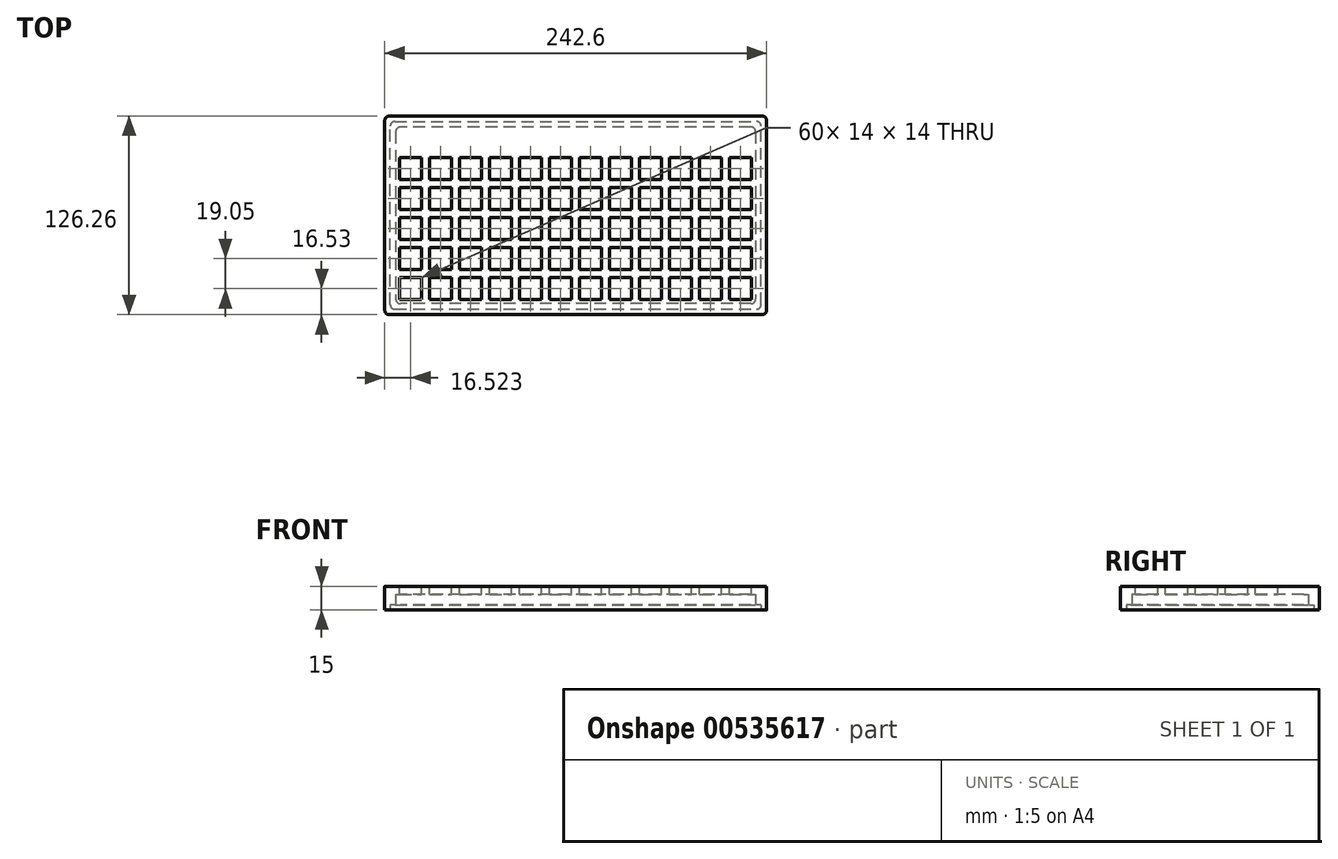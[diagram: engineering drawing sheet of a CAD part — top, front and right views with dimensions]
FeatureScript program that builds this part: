
annotation { "Feature Type Name" : "Feature", "Feature Type Description" : "" }
export const myFeature = defineFeature(function(context is Context, id is Id, definition is map)
    precondition{}
    {
        {
            var Q0;
            Q0=qCreatedBy(makeId("Top.planeOp"),FACE);
            var sketch = newSketch(context, id + "F0", { "sketchPlane" : qUnion([Q0])});
            skLineSegment(sketch, "E0", {"start": v(-121.3, 63.13) * mm, "end": v(121.3, 63.13) * mm});
            skLineSegment(sketch, "E1", {"start": v(121.3, 63.13) * mm, "end": v(121.3, -63.13) * mm});
            skLineSegment(sketch, "E2", {"start": v(121.3, -63.13) * mm, "end": v(-121.3, -63.13) * mm});
            skLineSegment(sketch, "E3", {"start": v(-121.3, -63.13) * mm, "end": v(-121.3, 63.13) * mm});
            skLineSegment(sketch, "E4", {"start": v(-111.78, -39.6) * mm, "end": v(-97.78, -39.6) * mm});
            skLineSegment(sketch, "E5", {"start": v(-97.78, -39.6) * mm, "end": v(-97.78, -53.6) * mm});
            skLineSegment(sketch, "E6", {"start": v(-97.78, -53.6) * mm, "end": v(-111.78, -53.6) * mm});
            skLineSegment(sketch, "E7", {"start": v(-111.78, -53.6) * mm, "end": v(-111.78, -39.6) * mm});
            skLineSegment(sketch, "E8", {"start": v(-92.73, -39.6) * mm, "end": v(-78.73, -39.6) * mm});
            skLineSegment(sketch, "E9", {"start": v(-78.73, -39.6) * mm, "end": v(-78.73, -53.6) * mm});
            skLineSegment(sketch, "E10", {"start": v(-78.73, -53.6) * mm, "end": v(-92.73, -53.6) * mm});
            skLineSegment(sketch, "E11", {"start": v(-92.73, -53.6) * mm, "end": v(-92.73, -39.6) * mm});
            skLineSegment(sketch, "E12", {"start": v(-73.68, -39.6) * mm, "end": v(-59.68, -39.6) * mm});
            skLineSegment(sketch, "E13", {"start": v(-59.68, -39.6) * mm, "end": v(-59.68, -53.6) * mm});
            skLineSegment(sketch, "E14", {"start": v(-59.68, -53.6) * mm, "end": v(-73.68, -53.6) * mm});
            skLineSegment(sketch, "E15", {"start": v(-73.68, -53.6) * mm, "end": v(-73.68, -39.6) * mm});
            skLineSegment(sketch, "E16", {"start": v(-54.63, -39.6) * mm, "end": v(-40.63, -39.6) * mm});
            skLineSegment(sketch, "E17", {"start": v(-40.63, -39.6) * mm, "end": v(-40.63, -53.6) * mm});
            skLineSegment(sketch, "E18", {"start": v(-40.63, -53.6) * mm, "end": v(-54.63, -53.6) * mm});
            skLineSegment(sketch, "E19", {"start": v(-54.63, -53.6) * mm, "end": v(-54.63, -39.6) * mm});
            skLineSegment(sketch, "E20", {"start": v(-35.58, -39.6) * mm, "end": v(-21.58, -39.6) * mm});
            skLineSegment(sketch, "E21", {"start": v(-21.58, -39.6) * mm, "end": v(-21.58, -53.6) * mm});
            skLineSegment(sketch, "E22", {"start": v(-21.58, -53.6) * mm, "end": v(-35.58, -53.6) * mm});
            skLineSegment(sketch, "E23", {"start": v(-35.58, -53.6) * mm, "end": v(-35.58, -39.6) * mm});
            skLineSegment(sketch, "E24", {"start": v(-16.53, -39.6) * mm, "end": v(-2.53, -39.6) * mm});
            skLineSegment(sketch, "E25", {"start": v(-2.53, -39.6) * mm, "end": v(-2.53, -53.6) * mm});
            skLineSegment(sketch, "E26", {"start": v(-2.53, -53.6) * mm, "end": v(-16.53, -53.6) * mm});
            skLineSegment(sketch, "E27", {"start": v(-16.53, -53.6) * mm, "end": v(-16.53, -39.6) * mm});
            skLineSegment(sketch, "E28", {"start": v(2.52, -39.6) * mm, "end": v(16.52, -39.6) * mm});
            skLineSegment(sketch, "E29", {"start": v(16.52, -39.6) * mm, "end": v(16.52, -53.6) * mm});
            skLineSegment(sketch, "E30", {"start": v(16.52, -53.6) * mm, "end": v(2.52, -53.6) * mm});
            skLineSegment(sketch, "E31", {"start": v(2.52, -53.6) * mm, "end": v(2.52, -39.6) * mm});
            skLineSegment(sketch, "E32", {"start": v(21.57, -39.6) * mm, "end": v(35.57, -39.6) * mm});
            skLineSegment(sketch, "E33", {"start": v(35.57, -39.6) * mm, "end": v(35.57, -53.6) * mm});
            skLineSegment(sketch, "E34", {"start": v(35.57, -53.6) * mm, "end": v(21.57, -53.6) * mm});
            skLineSegment(sketch, "E35", {"start": v(21.57, -53.6) * mm, "end": v(21.57, -39.6) * mm});
            skLineSegment(sketch, "E36", {"start": v(40.62, -39.6) * mm, "end": v(54.62, -39.6) * mm});
            skLineSegment(sketch, "E37", {"start": v(54.62, -39.6) * mm, "end": v(54.62, -53.6) * mm});
            skLineSegment(sketch, "E38", {"start": v(54.62, -53.6) * mm, "end": v(40.62, -53.6) * mm});
            skLineSegment(sketch, "E39", {"start": v(40.62, -53.6) * mm, "end": v(40.62, -39.6) * mm});
            skLineSegment(sketch, "E40", {"start": v(59.67, -39.6) * mm, "end": v(73.67, -39.6) * mm});
            skLineSegment(sketch, "E41", {"start": v(73.67, -39.6) * mm, "end": v(73.67, -53.6) * mm});
            skLineSegment(sketch, "E42", {"start": v(73.67, -53.6) * mm, "end": v(59.67, -53.6) * mm});
            skLineSegment(sketch, "E43", {"start": v(59.67, -53.6) * mm, "end": v(59.67, -39.6) * mm});
            skLineSegment(sketch, "E44", {"start": v(78.72, -39.6) * mm, "end": v(92.72, -39.6) * mm});
            skLineSegment(sketch, "E45", {"start": v(92.72, -39.6) * mm, "end": v(92.72, -53.6) * mm});
            skLineSegment(sketch, "E46", {"start": v(92.72, -53.6) * mm, "end": v(78.72, -53.6) * mm});
            skLineSegment(sketch, "E47", {"start": v(78.72, -53.6) * mm, "end": v(78.72, -39.6) * mm});
            skLineSegment(sketch, "E48", {"start": v(97.77, -39.6) * mm, "end": v(111.77, -39.6) * mm});
            skLineSegment(sketch, "E49", {"start": v(111.77, -39.6) * mm, "end": v(111.77, -53.6) * mm});
            skLineSegment(sketch, "E50", {"start": v(111.77, -53.6) * mm, "end": v(97.77, -53.6) * mm});
            skLineSegment(sketch, "E51", {"start": v(97.77, -53.6) * mm, "end": v(97.77, -39.6) * mm});
            skLineSegment(sketch, "E52", {"start": v(-111.78, -20.55) * mm, "end": v(-97.78, -20.55) * mm});
            skLineSegment(sketch, "E53", {"start": v(-97.78, -20.55) * mm, "end": v(-97.78, -34.55) * mm});
            skLineSegment(sketch, "E54", {"start": v(-97.78, -34.55) * mm, "end": v(-111.78, -34.55) * mm});
            skLineSegment(sketch, "E55", {"start": v(-111.78, -34.55) * mm, "end": v(-111.78, -20.55) * mm});
            skLineSegment(sketch, "E56", {"start": v(-92.73, -20.55) * mm, "end": v(-78.73, -20.55) * mm});
            skLineSegment(sketch, "E57", {"start": v(-78.73, -20.55) * mm, "end": v(-78.73, -34.55) * mm});
            skLineSegment(sketch, "E58", {"start": v(-78.73, -34.55) * mm, "end": v(-92.73, -34.55) * mm});
            skLineSegment(sketch, "E59", {"start": v(-92.73, -34.55) * mm, "end": v(-92.73, -20.55) * mm});
            skLineSegment(sketch, "E60", {"start": v(-73.68, -20.55) * mm, "end": v(-59.68, -20.55) * mm});
            skLineSegment(sketch, "E61", {"start": v(-59.68, -20.55) * mm, "end": v(-59.68, -34.55) * mm});
            skLineSegment(sketch, "E62", {"start": v(-59.68, -34.55) * mm, "end": v(-73.68, -34.55) * mm});
            skLineSegment(sketch, "E63", {"start": v(-73.68, -34.55) * mm, "end": v(-73.68, -20.55) * mm});
            skLineSegment(sketch, "E64", {"start": v(-54.63, -20.55) * mm, "end": v(-40.63, -20.55) * mm});
            skLineSegment(sketch, "E65", {"start": v(-40.63, -20.55) * mm, "end": v(-40.63, -34.55) * mm});
            skLineSegment(sketch, "E66", {"start": v(-40.63, -34.55) * mm, "end": v(-54.63, -34.55) * mm});
            skLineSegment(sketch, "E67", {"start": v(-54.63, -34.55) * mm, "end": v(-54.63, -20.55) * mm});
            skLineSegment(sketch, "E68", {"start": v(-35.58, -20.55) * mm, "end": v(-21.58, -20.55) * mm});
            skLineSegment(sketch, "E69", {"start": v(-21.58, -20.55) * mm, "end": v(-21.58, -34.55) * mm});
            skLineSegment(sketch, "E70", {"start": v(-21.58, -34.55) * mm, "end": v(-35.58, -34.55) * mm});
            skLineSegment(sketch, "E71", {"start": v(-35.58, -34.55) * mm, "end": v(-35.58, -20.55) * mm});
            skLineSegment(sketch, "E72", {"start": v(-16.53, -20.55) * mm, "end": v(-2.53, -20.55) * mm});
            skLineSegment(sketch, "E73", {"start": v(-2.53, -20.55) * mm, "end": v(-2.53, -34.55) * mm});
            skLineSegment(sketch, "E74", {"start": v(-2.53, -34.55) * mm, "end": v(-16.53, -34.55) * mm});
            skLineSegment(sketch, "E75", {"start": v(-16.53, -34.55) * mm, "end": v(-16.53, -20.55) * mm});
            skLineSegment(sketch, "E76", {"start": v(2.52, -20.55) * mm, "end": v(16.52, -20.55) * mm});
            skLineSegment(sketch, "E77", {"start": v(16.52, -20.55) * mm, "end": v(16.52, -34.55) * mm});
            skLineSegment(sketch, "E78", {"start": v(16.52, -34.55) * mm, "end": v(2.52, -34.55) * mm});
            skLineSegment(sketch, "E79", {"start": v(2.52, -34.55) * mm, "end": v(2.52, -20.55) * mm});
            skLineSegment(sketch, "E80", {"start": v(21.57, -20.55) * mm, "end": v(35.57, -20.55) * mm});
            skLineSegment(sketch, "E81", {"start": v(35.57, -20.55) * mm, "end": v(35.57, -34.55) * mm});
            skLineSegment(sketch, "E82", {"start": v(35.57, -34.55) * mm, "end": v(21.57, -34.55) * mm});
            skLineSegment(sketch, "E83", {"start": v(21.57, -34.55) * mm, "end": v(21.57, -20.55) * mm});
            skLineSegment(sketch, "E84", {"start": v(40.62, -20.55) * mm, "end": v(54.62, -20.55) * mm});
            skLineSegment(sketch, "E85", {"start": v(54.62, -20.55) * mm, "end": v(54.62, -34.55) * mm});
            skLineSegment(sketch, "E86", {"start": v(54.62, -34.55) * mm, "end": v(40.62, -34.55) * mm});
            skLineSegment(sketch, "E87", {"start": v(40.62, -34.55) * mm, "end": v(40.62, -20.55) * mm});
            skLineSegment(sketch, "E88", {"start": v(59.67, -20.55) * mm, "end": v(73.67, -20.55) * mm});
            skLineSegment(sketch, "E89", {"start": v(73.67, -20.55) * mm, "end": v(73.67, -34.55) * mm});
            skLineSegment(sketch, "E90", {"start": v(73.67, -34.55) * mm, "end": v(59.67, -34.55) * mm});
            skLineSegment(sketch, "E91", {"start": v(59.67, -34.55) * mm, "end": v(59.67, -20.55) * mm});
            skLineSegment(sketch, "E92", {"start": v(78.72, -20.55) * mm, "end": v(92.72, -20.55) * mm});
            skLineSegment(sketch, "E93", {"start": v(92.72, -20.55) * mm, "end": v(92.72, -34.55) * mm});
            skLineSegment(sketch, "E94", {"start": v(92.72, -34.55) * mm, "end": v(78.72, -34.55) * mm});
            skLineSegment(sketch, "E95", {"start": v(78.72, -34.55) * mm, "end": v(78.72, -20.55) * mm});
            skLineSegment(sketch, "E96", {"start": v(97.77, -20.55) * mm, "end": v(111.77, -20.55) * mm});
            skLineSegment(sketch, "E97", {"start": v(111.77, -20.55) * mm, "end": v(111.77, -34.55) * mm});
            skLineSegment(sketch, "E98", {"start": v(111.77, -34.55) * mm, "end": v(97.77, -34.55) * mm});
            skLineSegment(sketch, "E99", {"start": v(97.77, -34.55) * mm, "end": v(97.77, -20.55) * mm});
            skLineSegment(sketch, "E100", {"start": v(-111.78, -1.5) * mm, "end": v(-97.78, -1.5) * mm});
            skLineSegment(sketch, "E101", {"start": v(-97.78, -1.5) * mm, "end": v(-97.78, -15.5) * mm});
            skLineSegment(sketch, "E102", {"start": v(-97.78, -15.5) * mm, "end": v(-111.78, -15.5) * mm});
            skLineSegment(sketch, "E103", {"start": v(-111.78, -15.5) * mm, "end": v(-111.78, -1.5) * mm});
            skLineSegment(sketch, "E104", {"start": v(-92.73, -1.5) * mm, "end": v(-78.73, -1.5) * mm});
            skLineSegment(sketch, "E105", {"start": v(-78.73, -1.5) * mm, "end": v(-78.73, -15.5) * mm});
            skLineSegment(sketch, "E106", {"start": v(-78.73, -15.5) * mm, "end": v(-92.73, -15.5) * mm});
            skLineSegment(sketch, "E107", {"start": v(-92.73, -15.5) * mm, "end": v(-92.73, -1.5) * mm});
            skLineSegment(sketch, "E108", {"start": v(-73.68, -1.5) * mm, "end": v(-59.68, -1.5) * mm});
            skLineSegment(sketch, "E109", {"start": v(-59.68, -1.5) * mm, "end": v(-59.68, -15.5) * mm});
            skLineSegment(sketch, "E110", {"start": v(-59.68, -15.5) * mm, "end": v(-73.68, -15.5) * mm});
            skLineSegment(sketch, "E111", {"start": v(-73.68, -15.5) * mm, "end": v(-73.68, -1.5) * mm});
            skLineSegment(sketch, "E112", {"start": v(-54.63, -1.5) * mm, "end": v(-40.63, -1.5) * mm});
            skLineSegment(sketch, "E113", {"start": v(-40.63, -1.5) * mm, "end": v(-40.63, -15.5) * mm});
            skLineSegment(sketch, "E114", {"start": v(-40.63, -15.5) * mm, "end": v(-54.63, -15.5) * mm});
            skLineSegment(sketch, "E115", {"start": v(-54.63, -15.5) * mm, "end": v(-54.63, -1.5) * mm});
            skLineSegment(sketch, "E116", {"start": v(-35.58, -1.5) * mm, "end": v(-21.58, -1.5) * mm});
            skLineSegment(sketch, "E117", {"start": v(-21.58, -1.5) * mm, "end": v(-21.58, -15.5) * mm});
            skLineSegment(sketch, "E118", {"start": v(-21.58, -15.5) * mm, "end": v(-35.58, -15.5) * mm});
            skLineSegment(sketch, "E119", {"start": v(-35.58, -15.5) * mm, "end": v(-35.58, -1.5) * mm});
            skLineSegment(sketch, "E120", {"start": v(-16.53, -1.5) * mm, "end": v(-2.53, -1.5) * mm});
            skLineSegment(sketch, "E121", {"start": v(-2.53, -1.5) * mm, "end": v(-2.53, -15.5) * mm});
            skLineSegment(sketch, "E122", {"start": v(-2.53, -15.5) * mm, "end": v(-16.53, -15.5) * mm});
            skLineSegment(sketch, "E123", {"start": v(-16.53, -15.5) * mm, "end": v(-16.53, -1.5) * mm});
            skLineSegment(sketch, "E124", {"start": v(2.52, -1.5) * mm, "end": v(16.52, -1.5) * mm});
            skLineSegment(sketch, "E125", {"start": v(16.52, -1.5) * mm, "end": v(16.52, -15.5) * mm});
            skLineSegment(sketch, "E126", {"start": v(16.52, -15.5) * mm, "end": v(2.52, -15.5) * mm});
            skLineSegment(sketch, "E127", {"start": v(2.52, -15.5) * mm, "end": v(2.52, -1.5) * mm});
            skLineSegment(sketch, "E128", {"start": v(21.57, -1.5) * mm, "end": v(35.57, -1.5) * mm});
            skLineSegment(sketch, "E129", {"start": v(35.57, -1.5) * mm, "end": v(35.57, -15.5) * mm});
            skLineSegment(sketch, "E130", {"start": v(35.57, -15.5) * mm, "end": v(21.57, -15.5) * mm});
            skLineSegment(sketch, "E131", {"start": v(21.57, -15.5) * mm, "end": v(21.57, -1.5) * mm});
            skLineSegment(sketch, "E132", {"start": v(40.62, -1.5) * mm, "end": v(54.62, -1.5) * mm});
            skLineSegment(sketch, "E133", {"start": v(54.62, -1.5) * mm, "end": v(54.62, -15.5) * mm});
            skLineSegment(sketch, "E134", {"start": v(54.62, -15.5) * mm, "end": v(40.62, -15.5) * mm});
            skLineSegment(sketch, "E135", {"start": v(40.62, -15.5) * mm, "end": v(40.62, -1.5) * mm});
            skLineSegment(sketch, "E136", {"start": v(59.67, -1.5) * mm, "end": v(73.67, -1.5) * mm});
            skLineSegment(sketch, "E137", {"start": v(73.67, -1.5) * mm, "end": v(73.67, -15.5) * mm});
            skLineSegment(sketch, "E138", {"start": v(73.67, -15.5) * mm, "end": v(59.67, -15.5) * mm});
            skLineSegment(sketch, "E139", {"start": v(59.67, -15.5) * mm, "end": v(59.67, -1.5) * mm});
            skLineSegment(sketch, "E140", {"start": v(78.72, -1.5) * mm, "end": v(92.72, -1.5) * mm});
            skLineSegment(sketch, "E141", {"start": v(92.72, -1.5) * mm, "end": v(92.72, -15.5) * mm});
            skLineSegment(sketch, "E142", {"start": v(92.72, -15.5) * mm, "end": v(78.72, -15.5) * mm});
            skLineSegment(sketch, "E143", {"start": v(78.72, -15.5) * mm, "end": v(78.72, -1.5) * mm});
            skLineSegment(sketch, "E144", {"start": v(97.77, -1.5) * mm, "end": v(111.77, -1.5) * mm});
            skLineSegment(sketch, "E145", {"start": v(111.77, -1.5) * mm, "end": v(111.77, -15.5) * mm});
            skLineSegment(sketch, "E146", {"start": v(111.77, -15.5) * mm, "end": v(97.77, -15.5) * mm});
            skLineSegment(sketch, "E147", {"start": v(97.77, -15.5) * mm, "end": v(97.77, -1.5) * mm});
            skLineSegment(sketch, "E148", {"start": v(-111.78, 17.55) * mm, "end": v(-97.78, 17.55) * mm});
            skLineSegment(sketch, "E149", {"start": v(-97.78, 17.55) * mm, "end": v(-97.78, 3.55) * mm});
            skLineSegment(sketch, "E150", {"start": v(-97.78, 3.55) * mm, "end": v(-111.78, 3.55) * mm});
            skLineSegment(sketch, "E151", {"start": v(-111.78, 3.55) * mm, "end": v(-111.78, 17.55) * mm});
            skLineSegment(sketch, "E152", {"start": v(-92.73, 17.55) * mm, "end": v(-78.73, 17.55) * mm});
            skLineSegment(sketch, "E153", {"start": v(-78.73, 17.55) * mm, "end": v(-78.73, 3.55) * mm});
            skLineSegment(sketch, "E154", {"start": v(-78.73, 3.55) * mm, "end": v(-92.73, 3.55) * mm});
            skLineSegment(sketch, "E155", {"start": v(-92.73, 3.55) * mm, "end": v(-92.73, 17.55) * mm});
            skLineSegment(sketch, "E156", {"start": v(-73.68, 17.55) * mm, "end": v(-59.68, 17.55) * mm});
            skLineSegment(sketch, "E157", {"start": v(-59.68, 17.55) * mm, "end": v(-59.68, 3.55) * mm});
            skLineSegment(sketch, "E158", {"start": v(-59.68, 3.55) * mm, "end": v(-73.68, 3.55) * mm});
            skLineSegment(sketch, "E159", {"start": v(-73.68, 3.55) * mm, "end": v(-73.68, 17.55) * mm});
            skLineSegment(sketch, "E160", {"start": v(-54.63, 17.55) * mm, "end": v(-40.63, 17.55) * mm});
            skLineSegment(sketch, "E161", {"start": v(-40.63, 17.55) * mm, "end": v(-40.63, 3.55) * mm});
            skLineSegment(sketch, "E162", {"start": v(-40.63, 3.55) * mm, "end": v(-54.63, 3.55) * mm});
            skLineSegment(sketch, "E163", {"start": v(-54.63, 3.55) * mm, "end": v(-54.63, 17.55) * mm});
            skLineSegment(sketch, "E164", {"start": v(-35.58, 17.55) * mm, "end": v(-21.58, 17.55) * mm});
            skLineSegment(sketch, "E165", {"start": v(-21.58, 17.55) * mm, "end": v(-21.58, 3.55) * mm});
            skLineSegment(sketch, "E166", {"start": v(-21.58, 3.55) * mm, "end": v(-35.58, 3.55) * mm});
            skLineSegment(sketch, "E167", {"start": v(-35.58, 3.55) * mm, "end": v(-35.58, 17.55) * mm});
            skLineSegment(sketch, "E168", {"start": v(-16.53, 17.55) * mm, "end": v(-2.53, 17.55) * mm});
            skLineSegment(sketch, "E169", {"start": v(-2.53, 17.55) * mm, "end": v(-2.53, 3.55) * mm});
            skLineSegment(sketch, "E170", {"start": v(-2.53, 3.55) * mm, "end": v(-16.53, 3.55) * mm});
            skLineSegment(sketch, "E171", {"start": v(-16.53, 3.55) * mm, "end": v(-16.53, 17.55) * mm});
            skLineSegment(sketch, "E172", {"start": v(2.52, 17.55) * mm, "end": v(16.52, 17.55) * mm});
            skLineSegment(sketch, "E173", {"start": v(16.52, 17.55) * mm, "end": v(16.52, 3.55) * mm});
            skLineSegment(sketch, "E174", {"start": v(16.52, 3.55) * mm, "end": v(2.52, 3.55) * mm});
            skLineSegment(sketch, "E175", {"start": v(2.52, 3.55) * mm, "end": v(2.52, 17.55) * mm});
            skLineSegment(sketch, "E176", {"start": v(21.57, 17.55) * mm, "end": v(35.57, 17.55) * mm});
            skLineSegment(sketch, "E177", {"start": v(35.57, 17.55) * mm, "end": v(35.57, 3.55) * mm});
            skLineSegment(sketch, "E178", {"start": v(35.57, 3.55) * mm, "end": v(21.57, 3.55) * mm});
            skLineSegment(sketch, "E179", {"start": v(21.57, 3.55) * mm, "end": v(21.57, 17.55) * mm});
            skLineSegment(sketch, "E180", {"start": v(40.62, 17.55) * mm, "end": v(54.62, 17.55) * mm});
            skLineSegment(sketch, "E181", {"start": v(54.62, 17.55) * mm, "end": v(54.62, 3.55) * mm});
            skLineSegment(sketch, "E182", {"start": v(54.62, 3.55) * mm, "end": v(40.62, 3.55) * mm});
            skLineSegment(sketch, "E183", {"start": v(40.62, 3.55) * mm, "end": v(40.62, 17.55) * mm});
            skLineSegment(sketch, "E184", {"start": v(59.67, 17.55) * mm, "end": v(73.67, 17.55) * mm});
            skLineSegment(sketch, "E185", {"start": v(73.67, 17.55) * mm, "end": v(73.67, 3.55) * mm});
            skLineSegment(sketch, "E186", {"start": v(73.67, 3.55) * mm, "end": v(59.67, 3.55) * mm});
            skLineSegment(sketch, "E187", {"start": v(59.67, 3.55) * mm, "end": v(59.67, 17.55) * mm});
            skLineSegment(sketch, "E188", {"start": v(78.72, 17.55) * mm, "end": v(92.72, 17.55) * mm});
            skLineSegment(sketch, "E189", {"start": v(92.72, 17.55) * mm, "end": v(92.72, 3.55) * mm});
            skLineSegment(sketch, "E190", {"start": v(92.72, 3.55) * mm, "end": v(78.72, 3.55) * mm});
            skLineSegment(sketch, "E191", {"start": v(78.72, 3.55) * mm, "end": v(78.72, 17.55) * mm});
            skLineSegment(sketch, "E192", {"start": v(97.77, 17.55) * mm, "end": v(111.77, 17.55) * mm});
            skLineSegment(sketch, "E193", {"start": v(111.77, 17.55) * mm, "end": v(111.77, 3.55) * mm});
            skLineSegment(sketch, "E194", {"start": v(111.77, 3.55) * mm, "end": v(97.77, 3.55) * mm});
            skLineSegment(sketch, "E195", {"start": v(97.77, 3.55) * mm, "end": v(97.77, 17.55) * mm});
            skLineSegment(sketch, "E196", {"start": v(-111.78, 36.6) * mm, "end": v(-97.78, 36.6) * mm});
            skLineSegment(sketch, "E197", {"start": v(-97.78, 36.6) * mm, "end": v(-97.78, 22.6) * mm});
            skLineSegment(sketch, "E198", {"start": v(-97.78, 22.6) * mm, "end": v(-111.78, 22.6) * mm});
            skLineSegment(sketch, "E199", {"start": v(-111.78, 22.6) * mm, "end": v(-111.78, 36.6) * mm});
            skLineSegment(sketch, "E200", {"start": v(-92.73, 36.6) * mm, "end": v(-78.73, 36.6) * mm});
            skLineSegment(sketch, "E201", {"start": v(-78.73, 36.6) * mm, "end": v(-78.73, 22.6) * mm});
            skLineSegment(sketch, "E202", {"start": v(-78.73, 22.6) * mm, "end": v(-92.73, 22.6) * mm});
            skLineSegment(sketch, "E203", {"start": v(-92.73, 22.6) * mm, "end": v(-92.73, 36.6) * mm});
            skLineSegment(sketch, "E204", {"start": v(-73.68, 36.6) * mm, "end": v(-59.68, 36.6) * mm});
            skLineSegment(sketch, "E205", {"start": v(-59.68, 36.6) * mm, "end": v(-59.68, 22.6) * mm});
            skLineSegment(sketch, "E206", {"start": v(-59.68, 22.6) * mm, "end": v(-73.68, 22.6) * mm});
            skLineSegment(sketch, "E207", {"start": v(-73.68, 22.6) * mm, "end": v(-73.68, 36.6) * mm});
            skLineSegment(sketch, "E208", {"start": v(-54.63, 36.6) * mm, "end": v(-40.63, 36.6) * mm});
            skLineSegment(sketch, "E209", {"start": v(-40.63, 36.6) * mm, "end": v(-40.63, 22.6) * mm});
            skLineSegment(sketch, "E210", {"start": v(-40.63, 22.6) * mm, "end": v(-54.63, 22.6) * mm});
            skLineSegment(sketch, "E211", {"start": v(-54.63, 22.6) * mm, "end": v(-54.63, 36.6) * mm});
            skLineSegment(sketch, "E212", {"start": v(-35.58, 36.6) * mm, "end": v(-21.58, 36.6) * mm});
            skLineSegment(sketch, "E213", {"start": v(-21.58, 36.6) * mm, "end": v(-21.58, 22.6) * mm});
            skLineSegment(sketch, "E214", {"start": v(-21.58, 22.6) * mm, "end": v(-35.58, 22.6) * mm});
            skLineSegment(sketch, "E215", {"start": v(-35.58, 22.6) * mm, "end": v(-35.58, 36.6) * mm});
            skLineSegment(sketch, "E216", {"start": v(-16.53, 36.6) * mm, "end": v(-2.53, 36.6) * mm});
            skLineSegment(sketch, "E217", {"start": v(-2.53, 36.6) * mm, "end": v(-2.53, 22.6) * mm});
            skLineSegment(sketch, "E218", {"start": v(-2.53, 22.6) * mm, "end": v(-16.53, 22.6) * mm});
            skLineSegment(sketch, "E219", {"start": v(-16.53, 22.6) * mm, "end": v(-16.53, 36.6) * mm});
            skLineSegment(sketch, "E220", {"start": v(2.52, 36.6) * mm, "end": v(16.52, 36.6) * mm});
            skLineSegment(sketch, "E221", {"start": v(16.52, 36.6) * mm, "end": v(16.52, 22.6) * mm});
            skLineSegment(sketch, "E222", {"start": v(16.52, 22.6) * mm, "end": v(2.52, 22.6) * mm});
            skLineSegment(sketch, "E223", {"start": v(2.52, 22.6) * mm, "end": v(2.52, 36.6) * mm});
            skLineSegment(sketch, "E224", {"start": v(21.57, 36.6) * mm, "end": v(35.57, 36.6) * mm});
            skLineSegment(sketch, "E225", {"start": v(35.57, 36.6) * mm, "end": v(35.57, 22.6) * mm});
            skLineSegment(sketch, "E226", {"start": v(35.57, 22.6) * mm, "end": v(21.57, 22.6) * mm});
            skLineSegment(sketch, "E227", {"start": v(21.57, 22.6) * mm, "end": v(21.57, 36.6) * mm});
            skLineSegment(sketch, "E228", {"start": v(40.62, 36.6) * mm, "end": v(54.62, 36.6) * mm});
            skLineSegment(sketch, "E229", {"start": v(54.62, 36.6) * mm, "end": v(54.62, 22.6) * mm});
            skLineSegment(sketch, "E230", {"start": v(54.62, 22.6) * mm, "end": v(40.62, 22.6) * mm});
            skLineSegment(sketch, "E231", {"start": v(40.62, 22.6) * mm, "end": v(40.62, 36.6) * mm});
            skLineSegment(sketch, "E232", {"start": v(59.67, 36.6) * mm, "end": v(73.67, 36.6) * mm});
            skLineSegment(sketch, "E233", {"start": v(73.67, 36.6) * mm, "end": v(73.67, 22.6) * mm});
            skLineSegment(sketch, "E234", {"start": v(73.67, 22.6) * mm, "end": v(59.67, 22.6) * mm});
            skLineSegment(sketch, "E235", {"start": v(59.67, 22.6) * mm, "end": v(59.67, 36.6) * mm});
            skLineSegment(sketch, "E236", {"start": v(78.72, 36.6) * mm, "end": v(92.72, 36.6) * mm});
            skLineSegment(sketch, "E237", {"start": v(92.72, 36.6) * mm, "end": v(92.72, 22.6) * mm});
            skLineSegment(sketch, "E238", {"start": v(92.72, 22.6) * mm, "end": v(78.72, 22.6) * mm});
            skLineSegment(sketch, "E239", {"start": v(78.72, 22.6) * mm, "end": v(78.72, 36.6) * mm});
            skLineSegment(sketch, "E240", {"start": v(97.77, 36.6) * mm, "end": v(111.77, 36.6) * mm});
            skLineSegment(sketch, "E241", {"start": v(111.77, 36.6) * mm, "end": v(111.77, 22.6) * mm});
            skLineSegment(sketch, "E242", {"start": v(111.77, 22.6) * mm, "end": v(97.77, 22.6) * mm});
            skLineSegment(sketch, "E243", {"start": v(97.77, 22.6) * mm, "end": v(97.77, 36.6) * mm});
            skSolve(sketch);
        }
        {
            var Q0;
            Q0=makeQuery(id+"F0.imprint","IMPRINT",FACE,{"disambiguationData":[TD([[makeQuery(id+"F0.imprint","IMPRINT",EDGE,{"derivedFrom":sQuery(id+"F0.wireOp",EDGE,"E0")}),-1.0]])]});
            extrude(context, id + "F1", {"entities" : qUnion([Q0]), "oppositeDirection" : true, "depth" : 15 * mm, "offsetDistance" : 25 * mm});
        }
        {
            var Q0;
            Q0=makeQuery(id+"F1.opExtrude","SWEPT_EDGE",EDGE,{"disambiguationData":[OSD([sQuery(id+"F0.wireOp",EDGE,"E0"),sQuery(id+"F0.wireOp",EDGE,"E3")])]});
            var Q1;
            Q1=makeQuery(id+"F1.opExtrude","SWEPT_EDGE",EDGE,{"disambiguationData":[OSD([sQuery(id+"F0.wireOp",EDGE,"E0"),sQuery(id+"F0.wireOp",EDGE,"E1")])]});
            var Q2;
            Q2=makeQuery(id+"F1.opExtrude","SWEPT_EDGE",EDGE,{"disambiguationData":[OSD([sQuery(id+"F0.wireOp",EDGE,"E1"),sQuery(id+"F0.wireOp",EDGE,"E2")])]});
            var Q3;
            Q3=makeQuery(id+"F1.opExtrude","SWEPT_EDGE",EDGE,{"disambiguationData":[OSD([sQuery(id+"F0.wireOp",EDGE,"E2"),sQuery(id+"F0.wireOp",EDGE,"E3")])]});
            fillet(context, id + "F2", {"entities" : qUnion([Q0, Q1, Q2, Q3]), "radius" : 3 * mm, "tangentPropagation" : true, "allowEdgeOverflow" : false});
        }
        {
            var Q0;
            Q0=makeQuery(id+"F1.opExtrude","CAP_FACE",FACE,{"disambiguationData":[OSD([sQuery(id+"F0.wireOp",EDGE,"E0"),sQuery(id+"F0.wireOp",EDGE,"E1"),sQuery(id+"F0.wireOp",EDGE,"E2"),sQuery(id+"F0.wireOp",EDGE,"E3"),sQuery(id+"F0.wireOp",EDGE,"E4"),sQuery(id+"F0.wireOp",EDGE,"E5"),sQuery(id+"F0.wireOp",EDGE,"E6"),sQuery(id+"F0.wireOp",EDGE,"E7"),sQuery(id+"F0.wireOp",EDGE,"E8"),sQuery(id+"F0.wireOp",EDGE,"E9"),sQuery(id+"F0.wireOp",EDGE,"E10"),sQuery(id+"F0.wireOp",EDGE,"E11"),sQuery(id+"F0.wireOp",EDGE,"E12"),sQuery(id+"F0.wireOp",EDGE,"E13"),sQuery(id+"F0.wireOp",EDGE,"E14"),sQuery(id+"F0.wireOp",EDGE,"E15"),sQuery(id+"F0.wireOp",EDGE,"E16"),sQuery(id+"F0.wireOp",EDGE,"E17"),sQuery(id+"F0.wireOp",EDGE,"E18"),sQuery(id+"F0.wireOp",EDGE,"E19"),sQuery(id+"F0.wireOp",EDGE,"E20"),sQuery(id+"F0.wireOp",EDGE,"E21"),sQuery(id+"F0.wireOp",EDGE,"E22"),sQuery(id+"F0.wireOp",EDGE,"E23"),sQuery(id+"F0.wireOp",EDGE,"E24"),sQuery(id+"F0.wireOp",EDGE,"E25"),sQuery(id+"F0.wireOp",EDGE,"E26"),sQuery(id+"F0.wireOp",EDGE,"E27"),sQuery(id+"F0.wireOp",EDGE,"E28"),sQuery(id+"F0.wireOp",EDGE,"E29"),sQuery(id+"F0.wireOp",EDGE,"E30"),sQuery(id+"F0.wireOp",EDGE,"E31"),sQuery(id+"F0.wireOp",EDGE,"E32"),sQuery(id+"F0.wireOp",EDGE,"E33"),sQuery(id+"F0.wireOp",EDGE,"E34"),sQuery(id+"F0.wireOp",EDGE,"E35"),sQuery(id+"F0.wireOp",EDGE,"E36"),sQuery(id+"F0.wireOp",EDGE,"E37"),sQuery(id+"F0.wireOp",EDGE,"E38"),sQuery(id+"F0.wireOp",EDGE,"E39"),sQuery(id+"F0.wireOp",EDGE,"E40"),sQuery(id+"F0.wireOp",EDGE,"E41"),sQuery(id+"F0.wireOp",EDGE,"E42"),sQuery(id+"F0.wireOp",EDGE,"E43"),sQuery(id+"F0.wireOp",EDGE,"E44"),sQuery(id+"F0.wireOp",EDGE,"E45"),sQuery(id+"F0.wireOp",EDGE,"E46"),sQuery(id+"F0.wireOp",EDGE,"E47"),sQuery(id+"F0.wireOp",EDGE,"E48"),sQuery(id+"F0.wireOp",EDGE,"E49"),sQuery(id+"F0.wireOp",EDGE,"E50"),sQuery(id+"F0.wireOp",EDGE,"E51"),sQuery(id+"F0.wireOp",EDGE,"E52"),sQuery(id+"F0.wireOp",EDGE,"E53"),sQuery(id+"F0.wireOp",EDGE,"E54"),sQuery(id+"F0.wireOp",EDGE,"E55"),sQuery(id+"F0.wireOp",EDGE,"E56"),sQuery(id+"F0.wireOp",EDGE,"E57"),sQuery(id+"F0.wireOp",EDGE,"E58"),sQuery(id+"F0.wireOp",EDGE,"E59"),sQuery(id+"F0.wireOp",EDGE,"E60"),sQuery(id+"F0.wireOp",EDGE,"E61"),sQuery(id+"F0.wireOp",EDGE,"E62"),sQuery(id+"F0.wireOp",EDGE,"E63"),sQuery(id+"F0.wireOp",EDGE,"E64"),sQuery(id+"F0.wireOp",EDGE,"E65"),sQuery(id+"F0.wireOp",EDGE,"E66"),sQuery(id+"F0.wireOp",EDGE,"E67"),sQuery(id+"F0.wireOp",EDGE,"E68"),sQuery(id+"F0.wireOp",EDGE,"E69"),sQuery(id+"F0.wireOp",EDGE,"E70"),sQuery(id+"F0.wireOp",EDGE,"E71"),sQuery(id+"F0.wireOp",EDGE,"E72"),sQuery(id+"F0.wireOp",EDGE,"E73"),sQuery(id+"F0.wireOp",EDGE,"E74"),sQuery(id+"F0.wireOp",EDGE,"E75"),sQuery(id+"F0.wireOp",EDGE,"E76"),sQuery(id+"F0.wireOp",EDGE,"E77"),sQuery(id+"F0.wireOp",EDGE,"E78"),sQuery(id+"F0.wireOp",EDGE,"E79"),sQuery(id+"F0.wireOp",EDGE,"E80"),sQuery(id+"F0.wireOp",EDGE,"E81"),sQuery(id+"F0.wireOp",EDGE,"E82"),sQuery(id+"F0.wireOp",EDGE,"E83"),sQuery(id+"F0.wireOp",EDGE,"E84"),sQuery(id+"F0.wireOp",EDGE,"E85"),sQuery(id+"F0.wireOp",EDGE,"E86"),sQuery(id+"F0.wireOp",EDGE,"E87"),sQuery(id+"F0.wireOp",EDGE,"E88"),sQuery(id+"F0.wireOp",EDGE,"E89"),sQuery(id+"F0.wireOp",EDGE,"E90"),sQuery(id+"F0.wireOp",EDGE,"E91"),sQuery(id+"F0.wireOp",EDGE,"E92"),sQuery(id+"F0.wireOp",EDGE,"E93"),sQuery(id+"F0.wireOp",EDGE,"E94"),sQuery(id+"F0.wireOp",EDGE,"E95"),sQuery(id+"F0.wireOp",EDGE,"E96"),sQuery(id+"F0.wireOp",EDGE,"E97"),sQuery(id+"F0.wireOp",EDGE,"E98"),sQuery(id+"F0.wireOp",EDGE,"E99"),sQuery(id+"F0.wireOp",EDGE,"E100"),sQuery(id+"F0.wireOp",EDGE,"E101"),sQuery(id+"F0.wireOp",EDGE,"E102"),sQuery(id+"F0.wireOp",EDGE,"E103"),sQuery(id+"F0.wireOp",EDGE,"E104"),sQuery(id+"F0.wireOp",EDGE,"E105"),sQuery(id+"F0.wireOp",EDGE,"E106"),sQuery(id+"F0.wireOp",EDGE,"E107"),sQuery(id+"F0.wireOp",EDGE,"E108"),sQuery(id+"F0.wireOp",EDGE,"E109"),sQuery(id+"F0.wireOp",EDGE,"E110"),sQuery(id+"F0.wireOp",EDGE,"E111"),sQuery(id+"F0.wireOp",EDGE,"E112"),sQuery(id+"F0.wireOp",EDGE,"E113"),sQuery(id+"F0.wireOp",EDGE,"E114"),sQuery(id+"F0.wireOp",EDGE,"E115"),sQuery(id+"F0.wireOp",EDGE,"E116"),sQuery(id+"F0.wireOp",EDGE,"E117"),sQuery(id+"F0.wireOp",EDGE,"E118"),sQuery(id+"F0.wireOp",EDGE,"E119"),sQuery(id+"F0.wireOp",EDGE,"E120"),sQuery(id+"F0.wireOp",EDGE,"E121"),sQuery(id+"F0.wireOp",EDGE,"E122"),sQuery(id+"F0.wireOp",EDGE,"E123"),sQuery(id+"F0.wireOp",EDGE,"E124"),sQuery(id+"F0.wireOp",EDGE,"E125"),sQuery(id+"F0.wireOp",EDGE,"E126"),sQuery(id+"F0.wireOp",EDGE,"E127"),sQuery(id+"F0.wireOp",EDGE,"E128"),sQuery(id+"F0.wireOp",EDGE,"E129"),sQuery(id+"F0.wireOp",EDGE,"E130"),sQuery(id+"F0.wireOp",EDGE,"E131"),sQuery(id+"F0.wireOp",EDGE,"E132"),sQuery(id+"F0.wireOp",EDGE,"E133"),sQuery(id+"F0.wireOp",EDGE,"E134"),sQuery(id+"F0.wireOp",EDGE,"E135"),sQuery(id+"F0.wireOp",EDGE,"E136"),sQuery(id+"F0.wireOp",EDGE,"E137"),sQuery(id+"F0.wireOp",EDGE,"E138"),sQuery(id+"F0.wireOp",EDGE,"E139"),sQuery(id+"F0.wireOp",EDGE,"E140"),sQuery(id+"F0.wireOp",EDGE,"E141"),sQuery(id+"F0.wireOp",EDGE,"E142"),sQuery(id+"F0.wireOp",EDGE,"E143"),sQuery(id+"F0.wireOp",EDGE,"E144"),sQuery(id+"F0.wireOp",EDGE,"E145"),sQuery(id+"F0.wireOp",EDGE,"E146"),sQuery(id+"F0.wireOp",EDGE,"E147"),sQuery(id+"F0.wireOp",EDGE,"E148"),sQuery(id+"F0.wireOp",EDGE,"E149"),sQuery(id+"F0.wireOp",EDGE,"E150"),sQuery(id+"F0.wireOp",EDGE,"E151"),sQuery(id+"F0.wireOp",EDGE,"E152"),sQuery(id+"F0.wireOp",EDGE,"E153"),sQuery(id+"F0.wireOp",EDGE,"E154"),sQuery(id+"F0.wireOp",EDGE,"E155"),sQuery(id+"F0.wireOp",EDGE,"E156"),sQuery(id+"F0.wireOp",EDGE,"E157"),sQuery(id+"F0.wireOp",EDGE,"E158"),sQuery(id+"F0.wireOp",EDGE,"E159"),sQuery(id+"F0.wireOp",EDGE,"E160"),sQuery(id+"F0.wireOp",EDGE,"E161"),sQuery(id+"F0.wireOp",EDGE,"E162"),sQuery(id+"F0.wireOp",EDGE,"E163"),sQuery(id+"F0.wireOp",EDGE,"E164"),sQuery(id+"F0.wireOp",EDGE,"E165"),sQuery(id+"F0.wireOp",EDGE,"E166"),sQuery(id+"F0.wireOp",EDGE,"E167"),sQuery(id+"F0.wireOp",EDGE,"E168"),sQuery(id+"F0.wireOp",EDGE,"E169"),sQuery(id+"F0.wireOp",EDGE,"E170"),sQuery(id+"F0.wireOp",EDGE,"E171"),sQuery(id+"F0.wireOp",EDGE,"E172"),sQuery(id+"F0.wireOp",EDGE,"E173"),sQuery(id+"F0.wireOp",EDGE,"E174"),sQuery(id+"F0.wireOp",EDGE,"E175"),sQuery(id+"F0.wireOp",EDGE,"E176"),sQuery(id+"F0.wireOp",EDGE,"E177"),sQuery(id+"F0.wireOp",EDGE,"E178"),sQuery(id+"F0.wireOp",EDGE,"E179"),sQuery(id+"F0.wireOp",EDGE,"E180"),sQuery(id+"F0.wireOp",EDGE,"E181"),sQuery(id+"F0.wireOp",EDGE,"E182"),sQuery(id+"F0.wireOp",EDGE,"E183"),sQuery(id+"F0.wireOp",EDGE,"E184"),sQuery(id+"F0.wireOp",EDGE,"E185"),sQuery(id+"F0.wireOp",EDGE,"E186"),sQuery(id+"F0.wireOp",EDGE,"E187"),sQuery(id+"F0.wireOp",EDGE,"E188"),sQuery(id+"F0.wireOp",EDGE,"E189"),sQuery(id+"F0.wireOp",EDGE,"E190"),sQuery(id+"F0.wireOp",EDGE,"E191"),sQuery(id+"F0.wireOp",EDGE,"E192"),sQuery(id+"F0.wireOp",EDGE,"E193"),sQuery(id+"F0.wireOp",EDGE,"E194"),sQuery(id+"F0.wireOp",EDGE,"E195"),sQuery(id+"F0.wireOp",EDGE,"E196"),sQuery(id+"F0.wireOp",EDGE,"E197"),sQuery(id+"F0.wireOp",EDGE,"E198"),sQuery(id+"F0.wireOp",EDGE,"E199"),sQuery(id+"F0.wireOp",EDGE,"E200"),sQuery(id+"F0.wireOp",EDGE,"E201"),sQuery(id+"F0.wireOp",EDGE,"E202"),sQuery(id+"F0.wireOp",EDGE,"E203"),sQuery(id+"F0.wireOp",EDGE,"E204"),sQuery(id+"F0.wireOp",EDGE,"E205"),sQuery(id+"F0.wireOp",EDGE,"E206"),sQuery(id+"F0.wireOp",EDGE,"E207"),sQuery(id+"F0.wireOp",EDGE,"E208"),sQuery(id+"F0.wireOp",EDGE,"E209"),sQuery(id+"F0.wireOp",EDGE,"E210"),sQuery(id+"F0.wireOp",EDGE,"E211"),sQuery(id+"F0.wireOp",EDGE,"E212"),sQuery(id+"F0.wireOp",EDGE,"E213"),sQuery(id+"F0.wireOp",EDGE,"E214"),sQuery(id+"F0.wireOp",EDGE,"E215"),sQuery(id+"F0.wireOp",EDGE,"E216"),sQuery(id+"F0.wireOp",EDGE,"E217"),sQuery(id+"F0.wireOp",EDGE,"E218"),sQuery(id+"F0.wireOp",EDGE,"E219"),sQuery(id+"F0.wireOp",EDGE,"E220"),sQuery(id+"F0.wireOp",EDGE,"E221"),sQuery(id+"F0.wireOp",EDGE,"E222"),sQuery(id+"F0.wireOp",EDGE,"E223"),sQuery(id+"F0.wireOp",EDGE,"E224"),sQuery(id+"F0.wireOp",EDGE,"E225"),sQuery(id+"F0.wireOp",EDGE,"E226"),sQuery(id+"F0.wireOp",EDGE,"E227"),sQuery(id+"F0.wireOp",EDGE,"E228"),sQuery(id+"F0.wireOp",EDGE,"E229"),sQuery(id+"F0.wireOp",EDGE,"E230"),sQuery(id+"F0.wireOp",EDGE,"E231"),sQuery(id+"F0.wireOp",EDGE,"E232"),sQuery(id+"F0.wireOp",EDGE,"E233"),sQuery(id+"F0.wireOp",EDGE,"E234"),sQuery(id+"F0.wireOp",EDGE,"E235"),sQuery(id+"F0.wireOp",EDGE,"E236"),sQuery(id+"F0.wireOp",EDGE,"E237"),sQuery(id+"F0.wireOp",EDGE,"E238"),sQuery(id+"F0.wireOp",EDGE,"E239"),sQuery(id+"F0.wireOp",EDGE,"E240"),sQuery(id+"F0.wireOp",EDGE,"E241"),sQuery(id+"F0.wireOp",EDGE,"E242"),sQuery(id+"F0.wireOp",EDGE,"E243")])],"isStart":false});
            var sketch = newSketch(context, id + "F3", { "sketchPlane" : qUnion([Q0])});
            skLineSegment(sketch, "E244.bottom", {"start": v(111.3, -56.13) * mm, "end": v(-111.3, -56.13) * mm});
            skLineSegment(sketch, "E244.top", {"start": v(111.3, 56.13) * mm, "end": v(-111.3, 56.13) * mm});
            skLineSegment(sketch, "E244.left", {"start": v(114.3, -53.13) * mm, "end": v(114.3, 53.13) * mm});
            skLineSegment(sketch, "E244.right", {"start": v(-114.3, -53.13) * mm, "end": v(-114.3, 53.13) * mm});
            skPoint(sketch, "E244.middle", {"position": v(0, 0) * mm});
            skPoint(sketch, "E245.visualSharp", {"position": v(114.3, -56.13) * mm});
            skArc(sketch, "E245.filletArc", {"start": v(111.3, -56.13) * mm, "mid": v(113.42, -55.25) * mm, "end": v(114.3, -53.13) * mm});
            skPoint(sketch, "E246.visualSharp", {"position": v(-114.3, -56.13) * mm});
            skArc(sketch, "E246.filletArc", {"start": v(-114.3, -53.13) * mm, "mid": v(-113.42, -55.25) * mm, "end": v(-111.3, -56.13) * mm});
            skPoint(sketch, "E247.visualSharp", {"position": v(-114.3, 56.13) * mm});
            skArc(sketch, "E247.filletArc", {"start": v(-111.3, 56.13) * mm, "mid": v(-113.42, 55.25) * mm, "end": v(-114.3, 53.13) * mm});
            skPoint(sketch, "E248.visualSharp", {"position": v(114.3, 56.13) * mm});
            skArc(sketch, "E248.filletArc", {"start": v(114.3, 53.13) * mm, "mid": v(113.42, 55.25) * mm, "end": v(111.3, 56.13) * mm});
            skSolve(sketch);
        }
        {
            var Q0;
            Q0=makeQuery(id+"F3.imprint","IMPRINT",FACE,{"disambiguationData":[TD([[makeQuery(id+"F3.imprint","IMPRINT",EDGE,{"derivedFrom":sQuery(id+"F3.wireOp",EDGE,"E244.bottom")}),-1.0]])]});
            extrude(context, id + "F4", {"entities" : qUnion([Q0]), "operationType" : NewBodyOperationType.REMOVE, "oppositeDirection" : true, "depth" : 10 * mm, "offsetDistance" : 25 * mm});
        }
        {
            var Q0;
            Q0=makeQuery(id+"F1.opExtrude","CAP_FACE",FACE,{"disambiguationData":[OSD([sQuery(id+"F0.wireOp",EDGE,"E0"),sQuery(id+"F0.wireOp",EDGE,"E1"),sQuery(id+"F0.wireOp",EDGE,"E2"),sQuery(id+"F0.wireOp",EDGE,"E3"),sQuery(id+"F0.wireOp",EDGE,"E4"),sQuery(id+"F0.wireOp",EDGE,"E5"),sQuery(id+"F0.wireOp",EDGE,"E6"),sQuery(id+"F0.wireOp",EDGE,"E7"),sQuery(id+"F0.wireOp",EDGE,"E8"),sQuery(id+"F0.wireOp",EDGE,"E9"),sQuery(id+"F0.wireOp",EDGE,"E10"),sQuery(id+"F0.wireOp",EDGE,"E11"),sQuery(id+"F0.wireOp",EDGE,"E12"),sQuery(id+"F0.wireOp",EDGE,"E13"),sQuery(id+"F0.wireOp",EDGE,"E14"),sQuery(id+"F0.wireOp",EDGE,"E15"),sQuery(id+"F0.wireOp",EDGE,"E16"),sQuery(id+"F0.wireOp",EDGE,"E17"),sQuery(id+"F0.wireOp",EDGE,"E18"),sQuery(id+"F0.wireOp",EDGE,"E19"),sQuery(id+"F0.wireOp",EDGE,"E20"),sQuery(id+"F0.wireOp",EDGE,"E21"),sQuery(id+"F0.wireOp",EDGE,"E22"),sQuery(id+"F0.wireOp",EDGE,"E23"),sQuery(id+"F0.wireOp",EDGE,"E24"),sQuery(id+"F0.wireOp",EDGE,"E25"),sQuery(id+"F0.wireOp",EDGE,"E26"),sQuery(id+"F0.wireOp",EDGE,"E27"),sQuery(id+"F0.wireOp",EDGE,"E28"),sQuery(id+"F0.wireOp",EDGE,"E29"),sQuery(id+"F0.wireOp",EDGE,"E30"),sQuery(id+"F0.wireOp",EDGE,"E31"),sQuery(id+"F0.wireOp",EDGE,"E32"),sQuery(id+"F0.wireOp",EDGE,"E33"),sQuery(id+"F0.wireOp",EDGE,"E34"),sQuery(id+"F0.wireOp",EDGE,"E35"),sQuery(id+"F0.wireOp",EDGE,"E36"),sQuery(id+"F0.wireOp",EDGE,"E37"),sQuery(id+"F0.wireOp",EDGE,"E38"),sQuery(id+"F0.wireOp",EDGE,"E39"),sQuery(id+"F0.wireOp",EDGE,"E40"),sQuery(id+"F0.wireOp",EDGE,"E41"),sQuery(id+"F0.wireOp",EDGE,"E42"),sQuery(id+"F0.wireOp",EDGE,"E43"),sQuery(id+"F0.wireOp",EDGE,"E44"),sQuery(id+"F0.wireOp",EDGE,"E45"),sQuery(id+"F0.wireOp",EDGE,"E46"),sQuery(id+"F0.wireOp",EDGE,"E47"),sQuery(id+"F0.wireOp",EDGE,"E48"),sQuery(id+"F0.wireOp",EDGE,"E49"),sQuery(id+"F0.wireOp",EDGE,"E50"),sQuery(id+"F0.wireOp",EDGE,"E51"),sQuery(id+"F0.wireOp",EDGE,"E52"),sQuery(id+"F0.wireOp",EDGE,"E53"),sQuery(id+"F0.wireOp",EDGE,"E54"),sQuery(id+"F0.wireOp",EDGE,"E55"),sQuery(id+"F0.wireOp",EDGE,"E56"),sQuery(id+"F0.wireOp",EDGE,"E57"),sQuery(id+"F0.wireOp",EDGE,"E58"),sQuery(id+"F0.wireOp",EDGE,"E59"),sQuery(id+"F0.wireOp",EDGE,"E60"),sQuery(id+"F0.wireOp",EDGE,"E61"),sQuery(id+"F0.wireOp",EDGE,"E62"),sQuery(id+"F0.wireOp",EDGE,"E63"),sQuery(id+"F0.wireOp",EDGE,"E64"),sQuery(id+"F0.wireOp",EDGE,"E65"),sQuery(id+"F0.wireOp",EDGE,"E66"),sQuery(id+"F0.wireOp",EDGE,"E67"),sQuery(id+"F0.wireOp",EDGE,"E68"),sQuery(id+"F0.wireOp",EDGE,"E69"),sQuery(id+"F0.wireOp",EDGE,"E70"),sQuery(id+"F0.wireOp",EDGE,"E71"),sQuery(id+"F0.wireOp",EDGE,"E72"),sQuery(id+"F0.wireOp",EDGE,"E73"),sQuery(id+"F0.wireOp",EDGE,"E74"),sQuery(id+"F0.wireOp",EDGE,"E75"),sQuery(id+"F0.wireOp",EDGE,"E76"),sQuery(id+"F0.wireOp",EDGE,"E77"),sQuery(id+"F0.wireOp",EDGE,"E78"),sQuery(id+"F0.wireOp",EDGE,"E79"),sQuery(id+"F0.wireOp",EDGE,"E80"),sQuery(id+"F0.wireOp",EDGE,"E81"),sQuery(id+"F0.wireOp",EDGE,"E82"),sQuery(id+"F0.wireOp",EDGE,"E83"),sQuery(id+"F0.wireOp",EDGE,"E84"),sQuery(id+"F0.wireOp",EDGE,"E85"),sQuery(id+"F0.wireOp",EDGE,"E86"),sQuery(id+"F0.wireOp",EDGE,"E87"),sQuery(id+"F0.wireOp",EDGE,"E88"),sQuery(id+"F0.wireOp",EDGE,"E89"),sQuery(id+"F0.wireOp",EDGE,"E90"),sQuery(id+"F0.wireOp",EDGE,"E91"),sQuery(id+"F0.wireOp",EDGE,"E92"),sQuery(id+"F0.wireOp",EDGE,"E93"),sQuery(id+"F0.wireOp",EDGE,"E94"),sQuery(id+"F0.wireOp",EDGE,"E95"),sQuery(id+"F0.wireOp",EDGE,"E96"),sQuery(id+"F0.wireOp",EDGE,"E97"),sQuery(id+"F0.wireOp",EDGE,"E98"),sQuery(id+"F0.wireOp",EDGE,"E99"),sQuery(id+"F0.wireOp",EDGE,"E100"),sQuery(id+"F0.wireOp",EDGE,"E101"),sQuery(id+"F0.wireOp",EDGE,"E102"),sQuery(id+"F0.wireOp",EDGE,"E103"),sQuery(id+"F0.wireOp",EDGE,"E104"),sQuery(id+"F0.wireOp",EDGE,"E105"),sQuery(id+"F0.wireOp",EDGE,"E106"),sQuery(id+"F0.wireOp",EDGE,"E107"),sQuery(id+"F0.wireOp",EDGE,"E108"),sQuery(id+"F0.wireOp",EDGE,"E109"),sQuery(id+"F0.wireOp",EDGE,"E110"),sQuery(id+"F0.wireOp",EDGE,"E111"),sQuery(id+"F0.wireOp",EDGE,"E112"),sQuery(id+"F0.wireOp",EDGE,"E113"),sQuery(id+"F0.wireOp",EDGE,"E114"),sQuery(id+"F0.wireOp",EDGE,"E115"),sQuery(id+"F0.wireOp",EDGE,"E116"),sQuery(id+"F0.wireOp",EDGE,"E117"),sQuery(id+"F0.wireOp",EDGE,"E118"),sQuery(id+"F0.wireOp",EDGE,"E119"),sQuery(id+"F0.wireOp",EDGE,"E120"),sQuery(id+"F0.wireOp",EDGE,"E121"),sQuery(id+"F0.wireOp",EDGE,"E122"),sQuery(id+"F0.wireOp",EDGE,"E123"),sQuery(id+"F0.wireOp",EDGE,"E124"),sQuery(id+"F0.wireOp",EDGE,"E125"),sQuery(id+"F0.wireOp",EDGE,"E126"),sQuery(id+"F0.wireOp",EDGE,"E127"),sQuery(id+"F0.wireOp",EDGE,"E128"),sQuery(id+"F0.wireOp",EDGE,"E129"),sQuery(id+"F0.wireOp",EDGE,"E130"),sQuery(id+"F0.wireOp",EDGE,"E131"),sQuery(id+"F0.wireOp",EDGE,"E132"),sQuery(id+"F0.wireOp",EDGE,"E133"),sQuery(id+"F0.wireOp",EDGE,"E134"),sQuery(id+"F0.wireOp",EDGE,"E135"),sQuery(id+"F0.wireOp",EDGE,"E136"),sQuery(id+"F0.wireOp",EDGE,"E137"),sQuery(id+"F0.wireOp",EDGE,"E138"),sQuery(id+"F0.wireOp",EDGE,"E139"),sQuery(id+"F0.wireOp",EDGE,"E140"),sQuery(id+"F0.wireOp",EDGE,"E141"),sQuery(id+"F0.wireOp",EDGE,"E142"),sQuery(id+"F0.wireOp",EDGE,"E143"),sQuery(id+"F0.wireOp",EDGE,"E144"),sQuery(id+"F0.wireOp",EDGE,"E145"),sQuery(id+"F0.wireOp",EDGE,"E146"),sQuery(id+"F0.wireOp",EDGE,"E147"),sQuery(id+"F0.wireOp",EDGE,"E148"),sQuery(id+"F0.wireOp",EDGE,"E149"),sQuery(id+"F0.wireOp",EDGE,"E150"),sQuery(id+"F0.wireOp",EDGE,"E151"),sQuery(id+"F0.wireOp",EDGE,"E152"),sQuery(id+"F0.wireOp",EDGE,"E153"),sQuery(id+"F0.wireOp",EDGE,"E154"),sQuery(id+"F0.wireOp",EDGE,"E155"),sQuery(id+"F0.wireOp",EDGE,"E156"),sQuery(id+"F0.wireOp",EDGE,"E157"),sQuery(id+"F0.wireOp",EDGE,"E158"),sQuery(id+"F0.wireOp",EDGE,"E159"),sQuery(id+"F0.wireOp",EDGE,"E160"),sQuery(id+"F0.wireOp",EDGE,"E161"),sQuery(id+"F0.wireOp",EDGE,"E162"),sQuery(id+"F0.wireOp",EDGE,"E163"),sQuery(id+"F0.wireOp",EDGE,"E164"),sQuery(id+"F0.wireOp",EDGE,"E165"),sQuery(id+"F0.wireOp",EDGE,"E166"),sQuery(id+"F0.wireOp",EDGE,"E167"),sQuery(id+"F0.wireOp",EDGE,"E168"),sQuery(id+"F0.wireOp",EDGE,"E169"),sQuery(id+"F0.wireOp",EDGE,"E170"),sQuery(id+"F0.wireOp",EDGE,"E171"),sQuery(id+"F0.wireOp",EDGE,"E172"),sQuery(id+"F0.wireOp",EDGE,"E173"),sQuery(id+"F0.wireOp",EDGE,"E174"),sQuery(id+"F0.wireOp",EDGE,"E175"),sQuery(id+"F0.wireOp",EDGE,"E176"),sQuery(id+"F0.wireOp",EDGE,"E177"),sQuery(id+"F0.wireOp",EDGE,"E178"),sQuery(id+"F0.wireOp",EDGE,"E179"),sQuery(id+"F0.wireOp",EDGE,"E180"),sQuery(id+"F0.wireOp",EDGE,"E181"),sQuery(id+"F0.wireOp",EDGE,"E182"),sQuery(id+"F0.wireOp",EDGE,"E183"),sQuery(id+"F0.wireOp",EDGE,"E184"),sQuery(id+"F0.wireOp",EDGE,"E185"),sQuery(id+"F0.wireOp",EDGE,"E186"),sQuery(id+"F0.wireOp",EDGE,"E187"),sQuery(id+"F0.wireOp",EDGE,"E188"),sQuery(id+"F0.wireOp",EDGE,"E189"),sQuery(id+"F0.wireOp",EDGE,"E190"),sQuery(id+"F0.wireOp",EDGE,"E191"),sQuery(id+"F0.wireOp",EDGE,"E192"),sQuery(id+"F0.wireOp",EDGE,"E193"),sQuery(id+"F0.wireOp",EDGE,"E194"),sQuery(id+"F0.wireOp",EDGE,"E195"),sQuery(id+"F0.wireOp",EDGE,"E196"),sQuery(id+"F0.wireOp",EDGE,"E197"),sQuery(id+"F0.wireOp",EDGE,"E198"),sQuery(id+"F0.wireOp",EDGE,"E199"),sQuery(id+"F0.wireOp",EDGE,"E200"),sQuery(id+"F0.wireOp",EDGE,"E201"),sQuery(id+"F0.wireOp",EDGE,"E202"),sQuery(id+"F0.wireOp",EDGE,"E203"),sQuery(id+"F0.wireOp",EDGE,"E204"),sQuery(id+"F0.wireOp",EDGE,"E205"),sQuery(id+"F0.wireOp",EDGE,"E206"),sQuery(id+"F0.wireOp",EDGE,"E207"),sQuery(id+"F0.wireOp",EDGE,"E208"),sQuery(id+"F0.wireOp",EDGE,"E209"),sQuery(id+"F0.wireOp",EDGE,"E210"),sQuery(id+"F0.wireOp",EDGE,"E211"),sQuery(id+"F0.wireOp",EDGE,"E212"),sQuery(id+"F0.wireOp",EDGE,"E213"),sQuery(id+"F0.wireOp",EDGE,"E214"),sQuery(id+"F0.wireOp",EDGE,"E215"),sQuery(id+"F0.wireOp",EDGE,"E216"),sQuery(id+"F0.wireOp",EDGE,"E217"),sQuery(id+"F0.wireOp",EDGE,"E218"),sQuery(id+"F0.wireOp",EDGE,"E219"),sQuery(id+"F0.wireOp",EDGE,"E220"),sQuery(id+"F0.wireOp",EDGE,"E221"),sQuery(id+"F0.wireOp",EDGE,"E222"),sQuery(id+"F0.wireOp",EDGE,"E223"),sQuery(id+"F0.wireOp",EDGE,"E224"),sQuery(id+"F0.wireOp",EDGE,"E225"),sQuery(id+"F0.wireOp",EDGE,"E226"),sQuery(id+"F0.wireOp",EDGE,"E227"),sQuery(id+"F0.wireOp",EDGE,"E228"),sQuery(id+"F0.wireOp",EDGE,"E229"),sQuery(id+"F0.wireOp",EDGE,"E230"),sQuery(id+"F0.wireOp",EDGE,"E231"),sQuery(id+"F0.wireOp",EDGE,"E232"),sQuery(id+"F0.wireOp",EDGE,"E233"),sQuery(id+"F0.wireOp",EDGE,"E234"),sQuery(id+"F0.wireOp",EDGE,"E235"),sQuery(id+"F0.wireOp",EDGE,"E236"),sQuery(id+"F0.wireOp",EDGE,"E237"),sQuery(id+"F0.wireOp",EDGE,"E238"),sQuery(id+"F0.wireOp",EDGE,"E239"),sQuery(id+"F0.wireOp",EDGE,"E240"),sQuery(id+"F0.wireOp",EDGE,"E241"),sQuery(id+"F0.wireOp",EDGE,"E242"),sQuery(id+"F0.wireOp",EDGE,"E243")])],"isStart":false});
            var sketch = newSketch(context, id + "F5", { "sketchPlane" : qUnion([Q0])});
            skLineSegment(sketch, "E249.bottom", {"start": v(-114.8, 59.63) * mm, "end": v(114.8, 59.63) * mm});
            skLineSegment(sketch, "E249.top", {"start": v(-114.8, -59.63) * mm, "end": v(114.8, -59.63) * mm});
            skLineSegment(sketch, "E249.left", {"start": v(-117.8, 56.63) * mm, "end": v(-117.8, -56.63) * mm});
            skLineSegment(sketch, "E249.right", {"start": v(117.8, 56.63) * mm, "end": v(117.8, -56.63) * mm});
            skPoint(sketch, "E249.middle", {"position": v(0, 0) * mm});
            skPoint(sketch, "E250.visualSharp", {"position": v(-117.8, 59.63) * mm});
            skArc(sketch, "E250.filletArc", {"start": v(-114.8, 59.63) * mm, "mid": v(-116.92, 58.75) * mm, "end": v(-117.8, 56.63) * mm});
            skPoint(sketch, "E251.visualSharp", {"position": v(117.8, 59.63) * mm});
            skArc(sketch, "E251.filletArc", {"start": v(117.8, 56.63) * mm, "mid": v(116.92, 58.75) * mm, "end": v(114.8, 59.63) * mm});
            skPoint(sketch, "E252.visualSharp", {"position": v(117.8, -59.63) * mm});
            skArc(sketch, "E252.filletArc", {"start": v(114.8, -59.63) * mm, "mid": v(116.92, -58.75) * mm, "end": v(117.8, -56.63) * mm});
            skPoint(sketch, "E253.visualSharp", {"position": v(-117.8, -59.63) * mm});
            skArc(sketch, "E253.filletArc", {"start": v(-117.8, -56.63) * mm, "mid": v(-116.92, -58.75) * mm, "end": v(-114.8, -59.63) * mm});
            skSolve(sketch);
        }
        {
            var Q0;
            Q0=makeQuery(id+"F5.imprint","IMPRINT",FACE,{"disambiguationData":[TD([[makeQuery(id+"F5.imprint","IMPRINT",EDGE,{"derivedFrom":sQuery(id+"F5.wireOp",EDGE,"E249.bottom")}),-1.0]])]});
            extrude(context, id + "F6", {"entities" : qUnion([Q0]), "operationType" : NewBodyOperationType.REMOVE, "oppositeDirection" : true, "depth" : 3.2 * mm, "offsetDistance" : 25 * mm});
        }
    });
